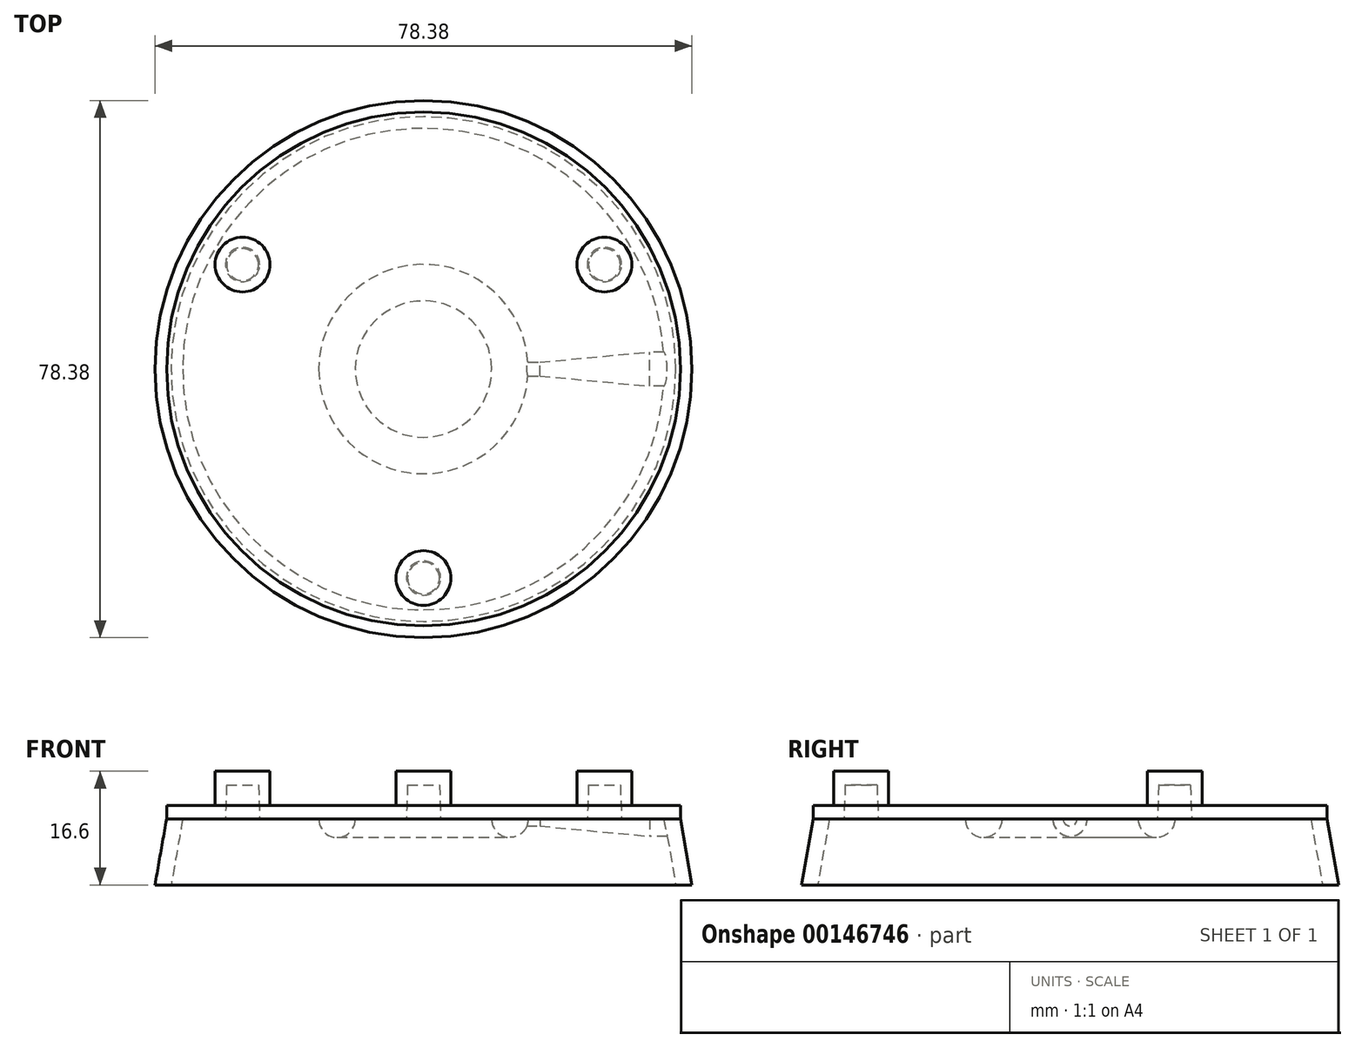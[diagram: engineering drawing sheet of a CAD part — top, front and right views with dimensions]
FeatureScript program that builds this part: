
annotation { "Feature Type Name" : "Feature", "Feature Type Description" : "" }
export const myFeature = defineFeature(function(context is Context, id is Id, definition is map)
    precondition{}
    {
        {
            var Q0;
            Q0=qCreatedBy(makeId("Front.planeOp"),FACE);
            var sketch = newSketch(context, id + "F0", { "sketchPlane" : qUnion([Q0])});
            skLineSegment(sketch, "E0", {"start": v(0, 0) * mm, "end": v(0, 36.8) * mm, "construction": true});
            skSolve(sketch);
        }
        {
            var Q0;
            Q0=qCreatedBy(makeId("Front.planeOp"),FACE);
            var sketch = newSketch(context, id + "F1", { "sketchPlane" : qUnion([Q0])});
            skLineSegment(sketch, "E1", {"start": v(-15.28, 0) * mm, "end": v(-9.95, 0) * mm});
            skArc(sketch, "E2", {"start": v(-15.28, 0) * mm, "mid": v(-12.61, -2.67) * mm, "end": v(-9.95, 0) * mm});
            skSolve(sketch);
        }
        {
            var Q0;
            Q0=qSketchRegion(id+"F1",true);
            var Q1;
            Q1=sQuery(id+"F0.wireOp",EDGE,"E0");
            revolve(context, id + "F2", {"entities" : qUnion([Q0]), "axis" : qUnion([Q1]), "revolveType" : RevolveType.FULL});
        }
        {
            var Q0;
            Q0=makeQuery(id+"F2.opRevolve","SWEPT_FACE",FACE,{"disambiguationData":[OSD([sQuery(id+"F1.wireOp",EDGE,"E1")])]});
            var sketch = newSketch(context, id + "F3", { "sketchPlane" : qUnion([Q0])});
            skCircle(sketch, "E3", {"center": v(0, 0) * mm, "radius": 37.5 * mm});
            skSolve(sketch);
        }
        {
            var Q0;
            Q0=qSketchRegion(id+"F3",true);
            extrude(context, id + "F4", {"entities" : qUnion([Q0]), "operationType" : NewBodyOperationType.ADD, "depth" : 2 * mm});
        }
        {
            var Q0;
            Q0=qCreatedBy(makeId("Right.planeOp"),FACE);
            var sketch = newSketch(context, id + "F5", { "sketchPlane" : qUnion([Q0])});
            skLineSegment(sketch, "E4", {"start": v(-35.14, 0) * mm, "end": v(-37.5, 0) * mm});
            skLineSegment(sketch, "E5", {"start": v(-37.5, 0) * mm, "end": v(-39.2, -9.6) * mm});
            skLineSegment(sketch, "E6", {"start": v(-39.2, -9.6) * mm, "end": v(-36.84, -9.6) * mm});
            skLineSegment(sketch, "E7", {"start": v(-36.84, -9.6) * mm, "end": v(-35.14, 0) * mm});
            skSolve(sketch);
        }
        {
            var Q0;
            Q0=qSketchRegion(id+"F5",true);
            var Q1;
            Q1=sQuery(id+"F0.wireOp",EDGE,"E0");
            revolve(context, id + "F6", {"operationType" : NewBodyOperationType.ADD, "entities" : qUnion([Q0]), "axis" : qUnion([Q1]), "revolveType" : RevolveType.FULL});
        }
        {
            var Q0;
            {var subQ0=sQuery(id+"F3.wireOp",EDGE,"E3");Q0=makeQuery(id+"F4.boolean.opBoolean","SPLIT",FACE,{"disambiguationData":[TD([makeQuery(id+"F2.opRevolve","SWEPT_FACE",FACE,{"disambiguationData":[OSD([sQuery(id+"F1.wireOp",EDGE,"E2")])]}),makeQuery(id+"F4.opExtrude","SWEPT_FACE",FACE,{"disambiguationData":[OSD([subQ0])]})])],"derivedFrom":makeQuery(id+"F4.opExtrude","CAP_FACE",FACE,{"disambiguationData":[OSD([subQ0])],"isStart":true})});}
            var sketch = newSketch(context, id + "F7", { "sketchPlane" : qUnion([Q0])});
            skCircle(sketch, "E8", {"center": v(0, 0) * mm, "radius": 30.5 * mm, "construction": true});
            skCircle(sketch, "E9", {"center": v(0, 30.5) * mm, "radius": 2.5 * mm});
            skCircle(sketch, "E10.1.0", {"center": v(-26.41, -15.25) * mm, "radius": 2.5 * mm});
            skCircle(sketch, "E10.2.0", {"center": v(26.41, -15.25) * mm, "radius": 2.5 * mm});
            skSolve(sketch);
        }
        {
            var Q0;
            Q0=makeQuery(id+"F4.opExtrude","CAP_FACE",FACE,{"disambiguationData":[OSD([sQuery(id+"F3.wireOp",EDGE,"E3")])],"isStart":false});
            var sketch = newSketch(context, id + "F8", { "sketchPlane" : qUnion([Q0])});
            skCircle(sketch, "E11", {"center": v(0, -30.5) * mm, "radius": 4 * mm});
            skCircle(sketch, "E12.1.0", {"center": v(26.41, 15.25) * mm, "radius": 4 * mm});
            skCircle(sketch, "E12.2.0", {"center": v(-26.41, 15.25) * mm, "radius": 4 * mm});
            skPoint(sketch, "E12.center", {"position": v(0, 0) * mm});
            skSolve(sketch);
        }
        {
            var Q0;
            Q0=qSketchRegion(id+"F8",true);
            extrude(context, id + "F9", {"entities" : qUnion([Q0]), "operationType" : NewBodyOperationType.ADD, "depth" : 5 * mm});
        }
        {
            var Q0;
            Q0=qSketchRegion(id+"F7",true);
            extrude(context, id + "F10", {"entities" : qUnion([Q0]), "operationType" : NewBodyOperationType.REMOVE, "oppositeDirection" : true, "depth" : 5 * mm, "hasDraft" : true, "draftAngle" : 2 * degree, "draftPullDirection" : true});
        }
        {
            var Q0;
            Q0=qCreatedBy(makeId("Right.planeOp"),FACE);
            cPlane(context, id + "F11", {"entities" : qUnion([Q0]), "cplaneType" : CPlaneType.OFFSET, "offset" : 33 * mm, "width" : 150 * mm, "height" : 150 * mm});
        }
        {
            var Q0;
            Q0=qCreatedBy(makeId("Right.planeOp"),FACE);
            cPlane(context, id + "F12", {"entities" : qUnion([Q0]), "cplaneType" : CPlaneType.OFFSET, "offset" : 17 * mm, "width" : 150 * mm, "height" : 150 * mm});
        }
        {
            var Q0;
            Q0=qCreatedBy(id+"F11.planeOp",FACE);
            var sketch = newSketch(context, id + "F13", { "sketchPlane" : qUnion([Q0])});
            skArc(sketch, "E13", {"start": v(-2.5, 0) * mm, "mid": v(0, -2.5) * mm, "end": v(2.5, 0) * mm});
            skLineSegment(sketch, "E14", {"start": v(-2.5, 0) * mm, "end": v(2.5, 0) * mm});
            skSolve(sketch);
        }
        {
            var Q0;
            Q0=qSketchRegion(id+"F13",true);
            var Q1;
            Q1=makeQuery(id+"F6.opRevolve","SWEPT_FACE",FACE,{"disambiguationData":[OSD([sQuery(id+"F5.wireOp",EDGE,"E7")])]});
            extrude(context, id + "F14", {"entities" : qUnion([Q0]), "operationType" : NewBodyOperationType.ADD, "endBound" : BoundingType.UP_TO_SURFACE, "endBoundEntityFace" : qUnion([Q1]), "depth" : 25 * mm});
        }
        {
            var Q0;
            Q0=qCreatedBy(id+"F12.planeOp",FACE);
            var sketch = newSketch(context, id + "F15", { "sketchPlane" : qUnion([Q0])});
            skArc(sketch, "E15", {"start": v(-1, 0) * mm, "mid": v(0, -1) * mm, "end": v(1, 0) * mm});
            skLineSegment(sketch, "E16", {"start": v(-1, 0) * mm, "end": v(1, 0) * mm});
            skSolve(sketch);
        }
        {
            var Q0;
            Q0=qSketchRegion(id+"F15",true);
            var Q1;
            Q1=makeQuery(id+"F2.opRevolve","SWEPT_FACE",FACE,{"disambiguationData":[OSD([sQuery(id+"F1.wireOp",EDGE,"E2")])]});
            extrude(context, id + "F16", {"entities" : qUnion([Q0]), "operationType" : NewBodyOperationType.ADD, "endBound" : BoundingType.UP_TO_SURFACE, "oppositeDirection" : true, "endBoundEntityFace" : qUnion([Q1]), "depth" : 25 * mm});
        }
        {
            var Q1;
            Q1=makeQuery(id+"F16.opExtrude","CAP_FACE",FACE,{"disambiguationData":[OSD([sQuery(id+"F15.wireOp",EDGE,"E15"),sQuery(id+"F15.wireOp",EDGE,"E16")])],"isStart":true});
            var Q2;
            Q2=makeQuery(id+"F14.opExtrude","CAP_FACE",FACE,{"disambiguationData":[OSD([sQuery(id+"F13.wireOp",EDGE,"E13"),sQuery(id+"F13.wireOp",EDGE,"E14")])],"isStart":true});
            loft(context, id + "F17", {"operationType" : NewBodyOperationType.ADD, "sheetProfilesArray" : [{ "sheetProfileEntities" : qUnion([Q1]) }, { "sheetProfileEntities" : qUnion([Q2]) }]});
        }
    });
